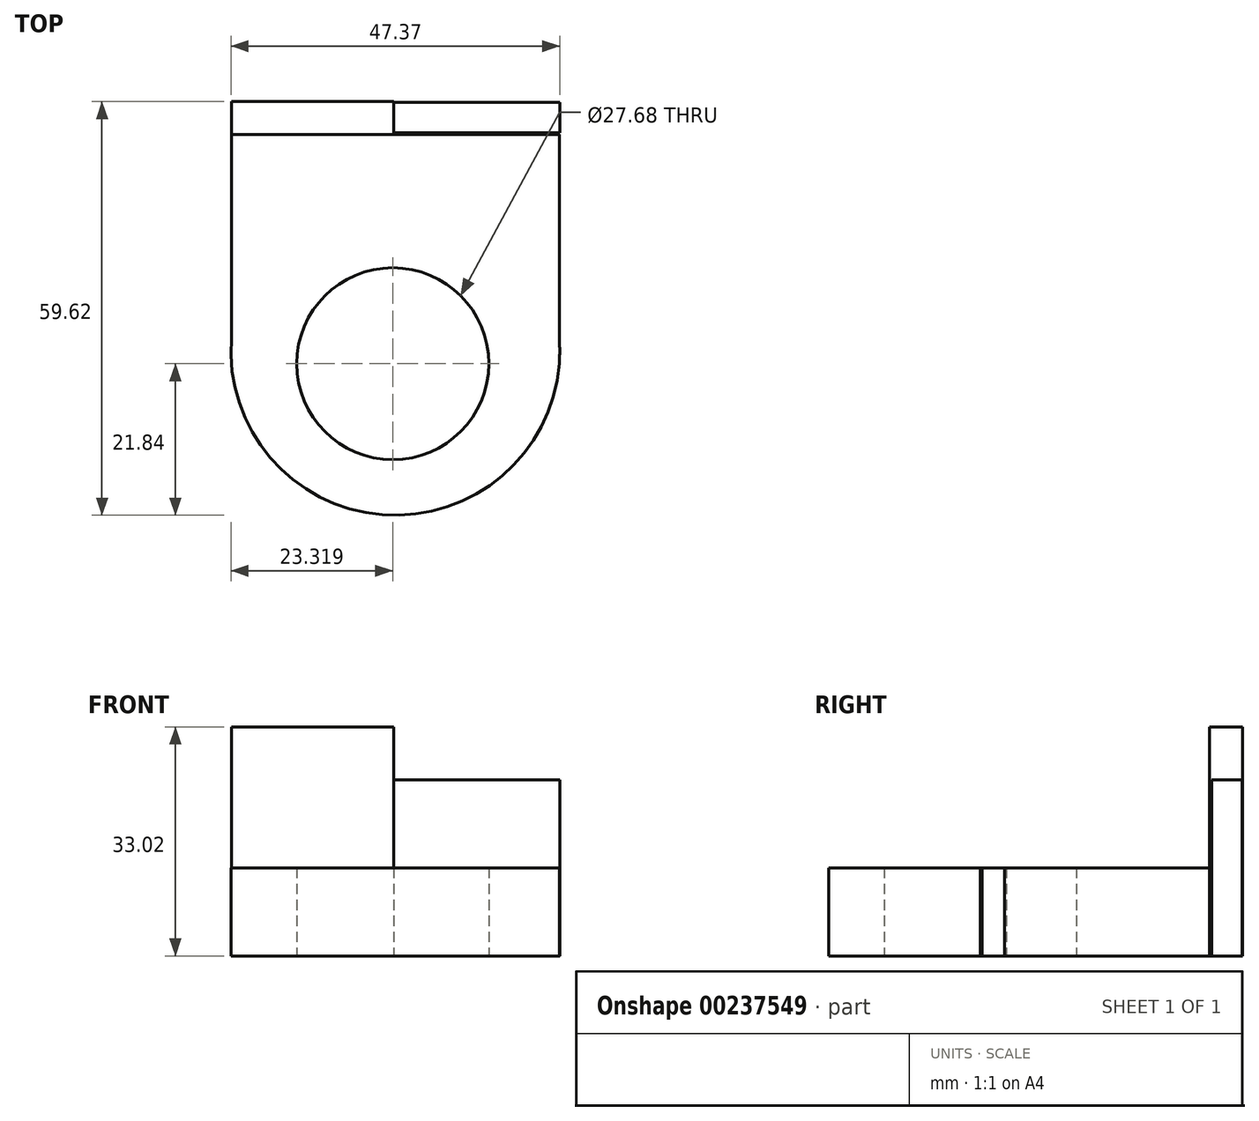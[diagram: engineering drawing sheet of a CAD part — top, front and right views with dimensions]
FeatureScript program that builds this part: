
annotation { "Feature Type Name" : "Feature", "Feature Type Description" : "" }
export const myFeature = defineFeature(function(context is Context, id is Id, definition is map)
    precondition{}
    {
        {
            var Q0;
            Q0=qCreatedBy(makeId("Top.planeOp"),FACE);
            var sketch = newSketch(context, id + "F0", { "sketchPlane" : qUnion([Q0])});
            skLineSegment(sketch, "E0.bottom", {"start": v(0, 0) * mm, "end": v(47.25, 0) * mm});
            skLineSegment(sketch, "E0.top", {"start": v(0, 33.02) * mm, "end": v(47.25, 33.02) * mm});
            skLineSegment(sketch, "E0.left", {"start": v(0, 0) * mm, "end": v(0, 33.02) * mm});
            skLineSegment(sketch, "E0.right", {"start": v(47.25, 0) * mm, "end": v(47.25, 33.02) * mm});
            skSolve(sketch);
        }
        {
            var Q0;
            Q0=qCreatedBy(makeId("Top.planeOp"),FACE);
            var sketch = newSketch(context, id + "F1", { "sketchPlane" : qUnion([Q0])});
            skCircle(sketch, "E1", {"center": v(23.62, 1.85) * mm, "radius": 23.69 * mm});
            skPoint(sketch, "E1.first.point", {"position": v(0, 0) * mm});
            skPoint(sketch, "E1.second.point", {"position": v(47.23, 0) * mm});
            skPoint(sketch, "E1.third.point", {"position": v(17.27, 24.67) * mm});
            skSolve(sketch);
        }
        {
            var Q0;
            Q0=makeQuery(id+"F0.imprint","IMPRINT",FACE,{"disambiguationData":[TD([[makeQuery(id+"F0.imprint","IMPRINT",EDGE,{"derivedFrom":sQuery(id+"F0.wireOp",EDGE,"E0.bottom")}),1.0]])]});
            extrude(context, id + "F2", {"entities" : qUnion([Q0]), "depth" : 12.7 * mm});
        }
        {
            var Q0;
            Q0=makeQuery(id+"F1.imprint","IMPRINT",FACE,{"disambiguationData":[TD([[makeQuery(id+"F1.imprint","IMPRINT",EDGE,{"derivedFrom":sQuery(id+"F1.wireOp",EDGE,"E1")}),1.0]])]});
            extrude(context, id + "F3", {"entities" : qUnion([Q0]), "operationType" : NewBodyOperationType.ADD, "depth" : 12.7 * mm});
        }
        {
            var Q0;
            Q0=qCreatedBy(makeId("Top.planeOp"),FACE);
            var sketch = newSketch(context, id + "F4", { "sketchPlane" : qUnion([Q0])});
            skCircle(sketch, "E2", {"center": v(23.25, 0) * mm, "radius": 13.84 * mm});
            skPoint(sketch, "E2.first.point", {"position": v(9.41, 0) * mm});
            skPoint(sketch, "E2.second.point", {"position": v(37.09, 0) * mm});
            skPoint(sketch, "E2.third.point", {"position": v(22.2, 13.8) * mm});
            skSolve(sketch);
        }
        {
            var Q0;
            Q0 = qSketchRegion(id + "F4", true);
            extrude(context, id + "F5", {"entities" : qUnion([Q0]), "operationType" : NewBodyOperationType.REMOVE, "endBound" : BoundingType.THROUGH_ALL, "depth" : 25.4 * mm});
        }
        {
            var Q0;
            Q0=qCreatedBy(makeId("Top.planeOp"),FACE);
            var sketch = newSketch(context, id + "F6", { "sketchPlane" : qUnion([Q0])});
            skLineSegment(sketch, "E3.bottom", {"start": v(0, 33.02) * mm, "end": v(23.37, 33.02) * mm});
            skLineSegment(sketch, "E3.top", {"start": v(0, 37.78) * mm, "end": v(23.37, 37.78) * mm});
            skLineSegment(sketch, "E3.left", {"start": v(0, 33.02) * mm, "end": v(0, 37.78) * mm});
            skLineSegment(sketch, "E3.right", {"start": v(23.37, 33.02) * mm, "end": v(23.37, 37.78) * mm});
            skSolve(sketch);
        }
        {
            var Q0;
            Q0=qCreatedBy(makeId("Top.planeOp"),FACE);
            var sketch = newSketch(context, id + "F7", { "sketchPlane" : qUnion([Q0])});
            skLineSegment(sketch, "E4.bottom", {"start": v(23.26, 33.3) * mm, "end": v(47.3, 33.3) * mm});
            skLineSegment(sketch, "E4.top", {"start": v(23.26, 37.68) * mm, "end": v(47.3, 37.68) * mm});
            skLineSegment(sketch, "E4.left", {"start": v(23.26, 33.3) * mm, "end": v(23.26, 37.68) * mm});
            skLineSegment(sketch, "E4.right", {"start": v(47.3, 33.3) * mm, "end": v(47.3, 37.68) * mm});
            skSolve(sketch);
        }
        {
            var Q0;
            Q0=makeQuery(id+"F6.imprint","IMPRINT",FACE,{"disambiguationData":[TD([[makeQuery(id+"F6.imprint","IMPRINT",EDGE,{"derivedFrom":sQuery(id+"F6.wireOp",EDGE,"E3.bottom")}),1.0]])]});
            extrude(context, id + "F8", {"entities" : qUnion([Q0]), "operationType" : NewBodyOperationType.ADD, "depth" : 33.02 * mm});
        }
        {
            var Q0;
            Q0=makeQuery(id+"F7.imprint","IMPRINT",FACE,{"disambiguationData":[TD([[makeQuery(id+"F7.imprint","IMPRINT",EDGE,{"derivedFrom":sQuery(id+"F7.wireOp",EDGE,"E4.bottom")}),1.0]])]});
            extrude(context, id + "F9", {"entities" : qUnion([Q0]), "operationType" : NewBodyOperationType.ADD, "depth" : 25.4 * mm});
        }
    });
